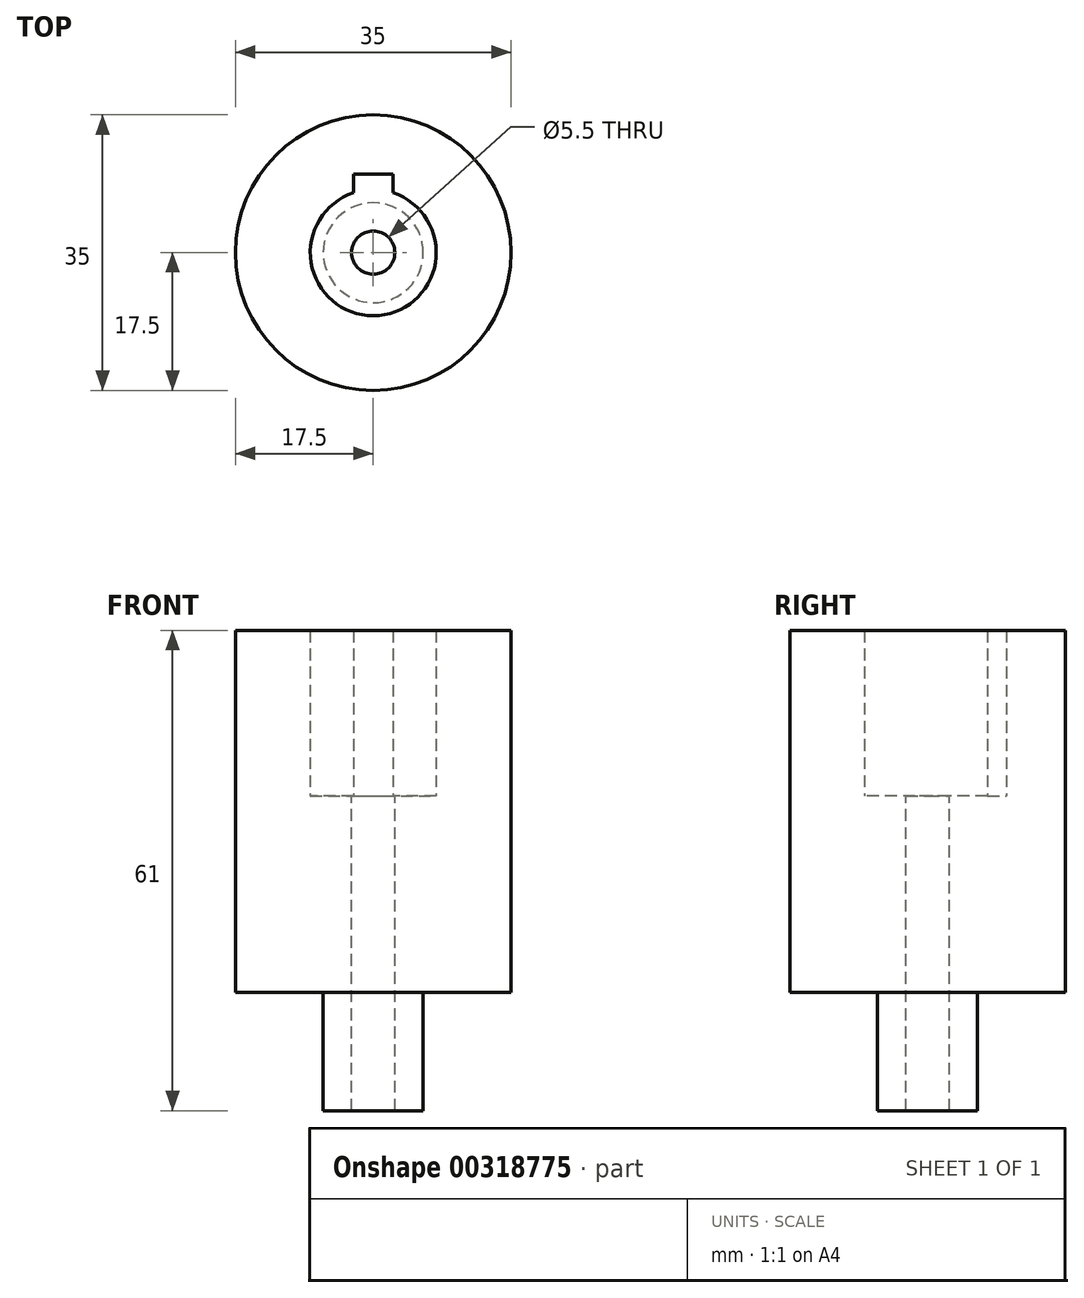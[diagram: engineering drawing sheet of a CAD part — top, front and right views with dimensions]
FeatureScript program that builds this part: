
annotation { "Feature Type Name" : "Feature", "Feature Type Description" : "" }
export const myFeature = defineFeature(function(context is Context, id is Id, definition is map)
    precondition{}
    {
        {
            var Q0;
            Q0=qCreatedBy(makeId("Top.planeOp"),FACE);
            var sketch = newSketch(context, id + "F0", { "sketchPlane" : qUnion([Q0])});
            skArc(sketch, "E0", {"start": v(-2.5, 7.6) * mm, "mid": v(0, -8) * mm, "end": v(2.5, 7.6) * mm});
            skCircle(sketch, "E1", {"center": v(0, 0) * mm, "radius": 17.5 * mm});
            skLineSegment(sketch, "E2.top", {"start": v(-2.5, 10) * mm, "end": v(2.5, 10) * mm});
            skLineSegment(sketch, "E2.left", {"start": v(-2.5, 7.6) * mm, "end": v(-2.5, 10) * mm});
            skLineSegment(sketch, "E2.right", {"start": v(2.5, 7.6) * mm, "end": v(2.5, 10) * mm});
            skPoint(sketch, "E3.orphan", {"position": v(2.5, 0) * mm});
            skPoint(sketch, "E2.bottom.start.orphan", {"position": v(-2.5, 0) * mm});
            skSolve(sketch);
        }
        {
            var Q0;
            Q0=makeQuery(id+"F0.imprint","IMPRINT",FACE,{"disambiguationData":[TD([[makeQuery(id+"F0.imprint","IMPRINT",EDGE,{"derivedFrom":sQuery(id+"F0.wireOp",EDGE,"E0")}),-1.0]])]});
            extrude(context, id + "F1", {"entities" : qUnion([Q0]), "depth" : 21 * mm, "hasSecondDirection" : true, "secondDirectionOppositeDirection" : true, "secondDirectionDepth" : 25 * mm, "offsetDistance" : 25 * mm, "symmetric" : true});
        }
        {
            var Q0;
            Q0=makeQuery(id+"F1.opExtrude","CAP_FACE",FACE,{"disambiguationData":[OSD([sQuery(id+"F0.wireOp",EDGE,"E0"),sQuery(id+"F0.wireOp",EDGE,"E1"),sQuery(id+"F0.wireOp",EDGE,"E2.top"),sQuery(id+"F0.wireOp",EDGE,"E2.left"),sQuery(id+"F0.wireOp",EDGE,"E2.right")])],"isStart":true});
            var sketch = newSketch(context, id + "F2", { "sketchPlane" : qUnion([Q0])});
            skCircle(sketch, "E4", {"center": v(0, 0) * mm, "radius": 17.5 * mm});
            skCircle(sketch, "E5", {"center": v(0, 0) * mm, "radius": 2.75 * mm});
            skSolve(sketch);
        }
        {
            var Q0;
            Q0=makeQuery(id+"F2.imprint","IMPRINT",FACE,{"disambiguationData":[TD([[makeQuery(id+"F2.imprint","IMPRINT",EDGE,{"derivedFrom":sQuery(id+"F2.wireOp",EDGE,"E4")}),-1.0]])]});
            var Q1;
            Q1=makeQuery(id+"F2.imprint","IMPRINT",FACE,{"disambiguationData":[TD([[makeQuery(id+"F2.imprint","IMPRINT",EDGE,{"derivedFrom":makeQuery(id+"F1.opExtrude","CAP_EDGE",EDGE,{"disambiguationData":[OSD([sQuery(id+"F0.wireOp",EDGE,"E0")])],"isStart":true})}),-1.0]])]});
            extrude(context, id + "F3", {"entities" : qUnion([Q0, Q1]), "operationType" : NewBodyOperationType.ADD, "offsetDistance" : 25 * mm, "depth" : 25 * mm});
        }
        {
            var Q0;
            Q0=makeQuery(id+"F3.opExtrude","CAP_FACE",FACE,{"disambiguationData":[OSD([sQuery(id+"F2.wireOp",EDGE,"E4"),sQuery(id+"F2.wireOp",EDGE,"E5")])],"isStart":false});
            var sketch = newSketch(context, id + "F4", { "sketchPlane" : qUnion([Q0])});
            skCircle(sketch, "E6", {"center": v(0, 0) * mm, "radius": 6.35 * mm});
            skCircle(sketch, "E7", {"center": v(0, 0) * mm, "radius": 2.75 * mm});
            skSolve(sketch);
        }
        {
            var Q0;
            Q0=makeQuery(id+"F4.imprint","IMPRINT",FACE,{"disambiguationData":[TD([[makeQuery(id+"F4.imprint","IMPRINT",EDGE,{"derivedFrom":sQuery(id+"F4.wireOp",EDGE,"E6")}),1.0]])]});
            extrude(context, id + "F5", {"entities" : qUnion([Q0]), "operationType" : NewBodyOperationType.ADD, "depth" : 15 * mm, "offsetDistance" : 25 * mm});
        }
    });
